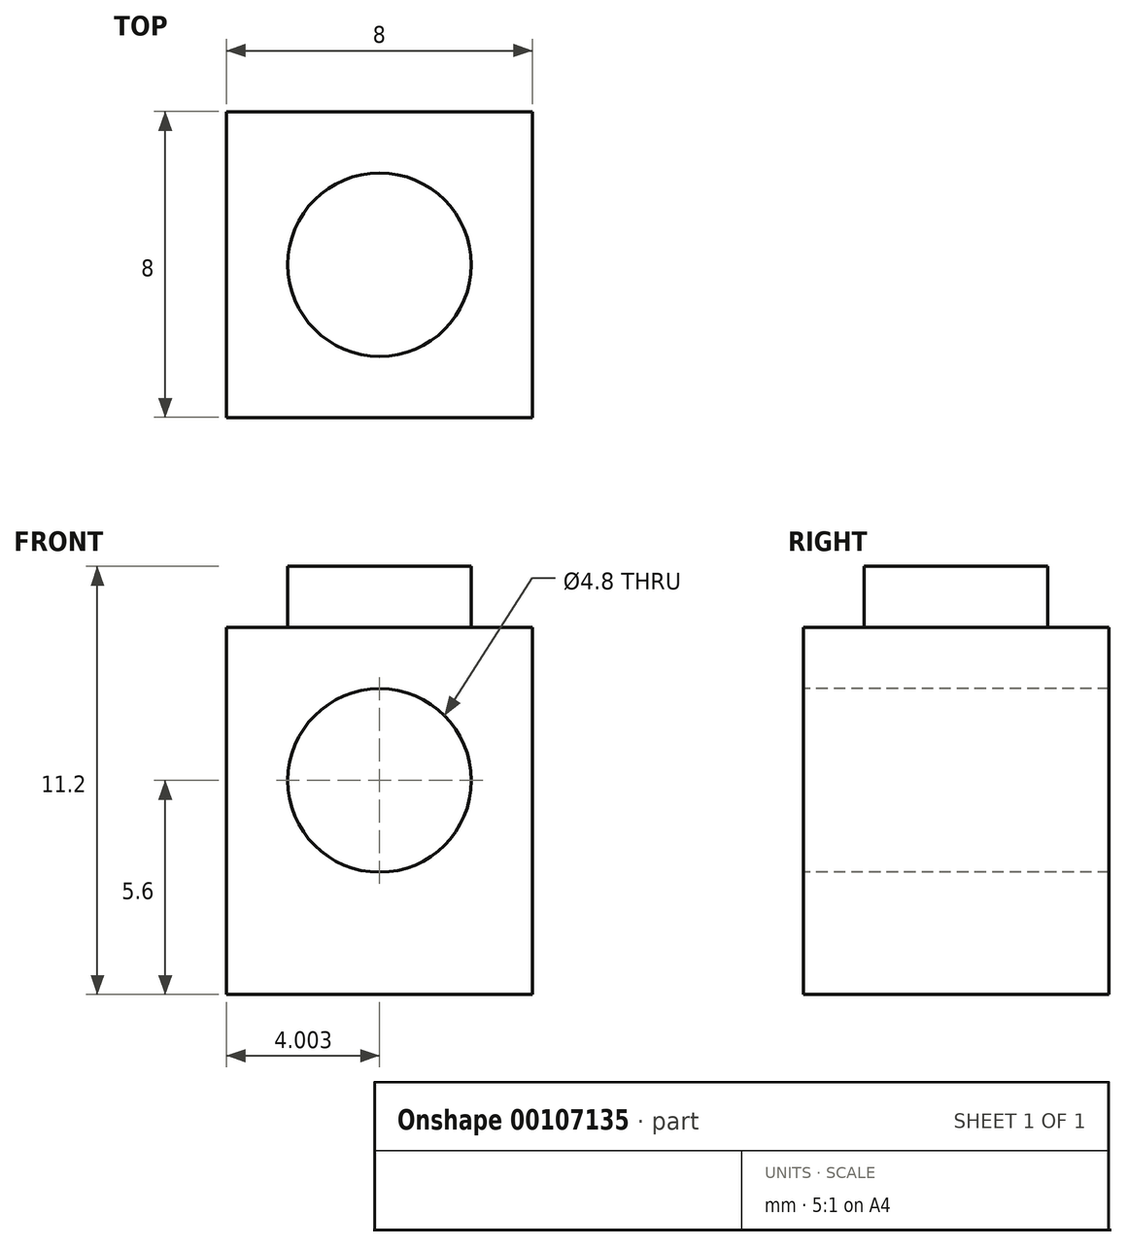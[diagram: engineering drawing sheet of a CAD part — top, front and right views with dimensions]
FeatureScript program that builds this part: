
annotation { "Feature Type Name" : "Feature", "Feature Type Description" : "" }
export const myFeature = defineFeature(function(context is Context, id is Id, definition is map)
    precondition{}
    {
        {
            var Q0;
            Q0=qCreatedBy(makeId("Top.planeOp"),FACE);
            var sketch = newSketch(context, id + "F0", { "sketchPlane" : qUnion([Q0])});
            skLineSegment(sketch, "E0.bottom", {"start": v(1.5, 0.57) * mm, "end": v(9.5, 0.57) * mm});
            skLineSegment(sketch, "E0.top", {"start": v(1.5, -7.43) * mm, "end": v(9.5, -7.43) * mm});
            skLineSegment(sketch, "E0.left", {"start": v(1.5, 0.57) * mm, "end": v(1.5, -7.43) * mm});
            skLineSegment(sketch, "E0.right", {"start": v(9.5, 0.57) * mm, "end": v(9.5, -7.43) * mm});
            skSolve(sketch);
        }
        {
            var Q0;
            Q0 = qSketchRegion(id + "F0", true);
            extrude(context, id + "F1", {"entities" : qUnion([Q0]), "depth" : 9.6 * mm});
        }
        {
            var Q0;
            Q0=makeQuery(id+"F1.opExtrude","SWEPT_FACE",FACE,{"disambiguationData":[OSD([sQuery(id+"F0.wireOp",EDGE,"E0.top")])]});
            var sketch = newSketch(context, id + "F2", { "sketchPlane" : qUnion([Q0])});
            skPoint(sketch, "E1.endSnap0", {"position": v(5.5, 0) * mm});
            skLineSegment(sketch, "E2", {"start": v(5.5, 0) * mm, "end": v(5.5, 5.6) * mm, "construction": true});
            skCircle(sketch, "E3", {"center": v(5.5, 5.6) * mm, "radius": 2.4 * mm});
            skSolve(sketch);
        }
        {
            var Q0;
            Q0=makeQuery(id+"F2.imprint","IMPRINT",FACE,{"disambiguationData":[TD([[makeQuery(id+"F2.imprint","IMPRINT",EDGE,{"derivedFrom":sQuery(id+"F2.wireOp",EDGE,"E3")}),1.0]])]});
            extrude(context, id + "F3", {"entities" : qUnion([Q0]), "operationType" : NewBodyOperationType.REMOVE, "oppositeDirection" : true, "depth" : 25 * mm});
        }
        {
            var Q0;
            Q0=makeQuery(id+"F1.opExtrude","CAP_FACE",FACE,{"disambiguationData":[OSD([sQuery(id+"F0.wireOp",EDGE,"E0.bottom"),sQuery(id+"F0.wireOp",EDGE,"E0.top"),sQuery(id+"F0.wireOp",EDGE,"E0.left"),sQuery(id+"F0.wireOp",EDGE,"E0.right")])],"isStart":false});
            var sketch = newSketch(context, id + "F4", { "sketchPlane" : qUnion([Q0])});
            skLineSegment(sketch, "E4", {"start": v(5.5, -3.43) * mm, "end": v(1.5, -3.43) * mm, "construction": true});
            skCircle(sketch, "E5", {"center": v(5.5, -3.43) * mm, "radius": 2.4 * mm});
            skSolve(sketch);
        }
        {
            var Q0;
            Q0 = qSketchRegion(id + "F4", true);
            extrude(context, id + "F5", {"entities" : qUnion([Q0]), "operationType" : NewBodyOperationType.ADD, "depth" : 1.6 * mm});
        }
    });
